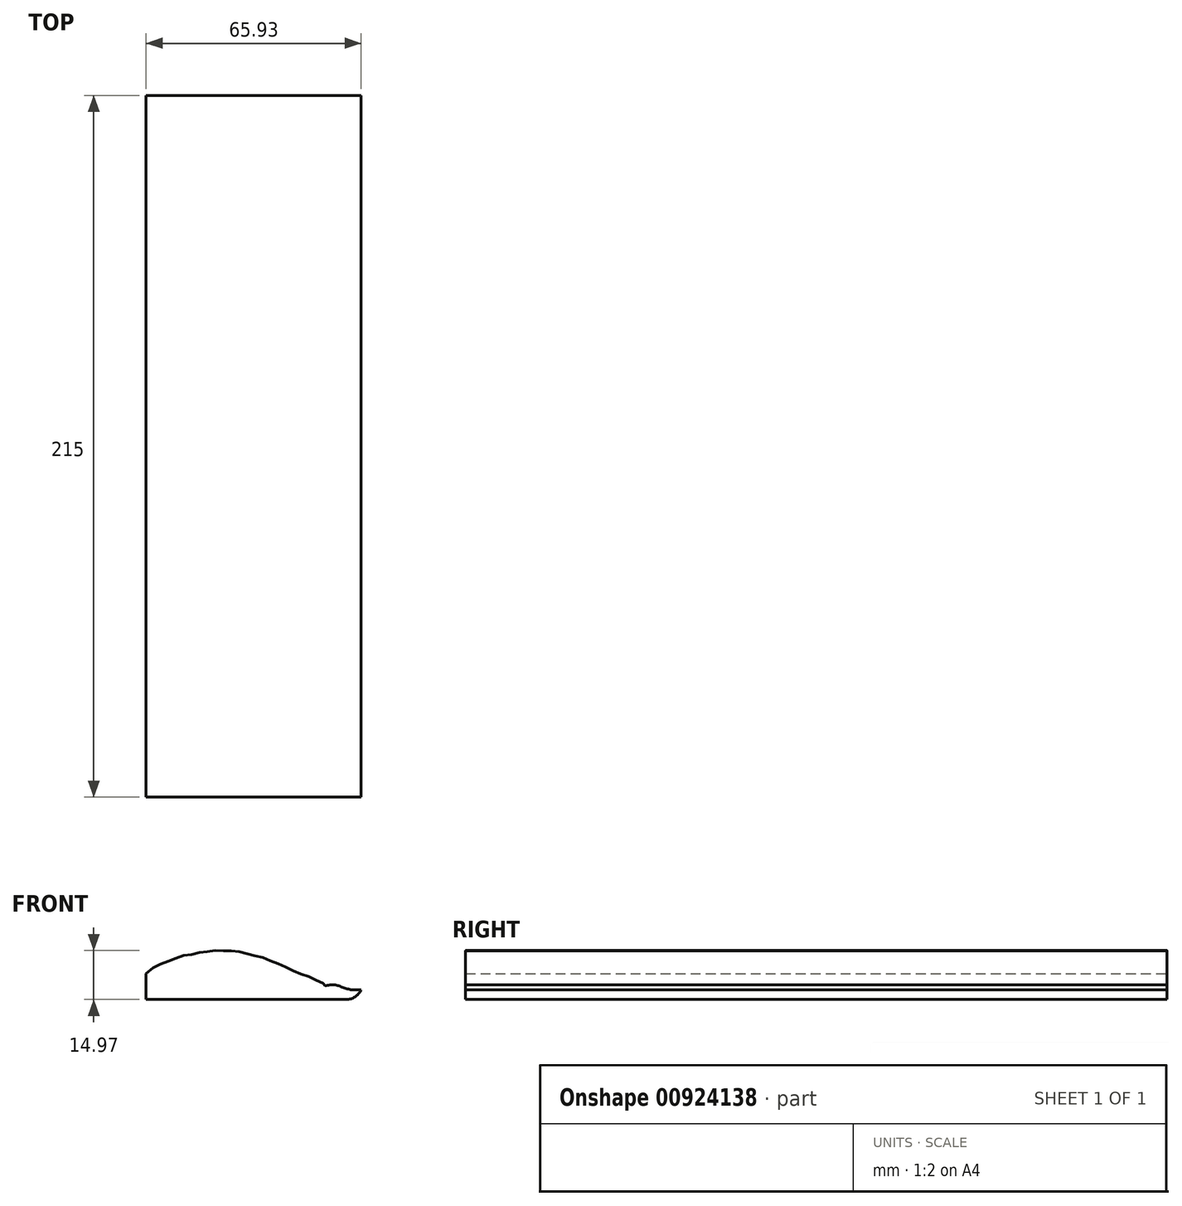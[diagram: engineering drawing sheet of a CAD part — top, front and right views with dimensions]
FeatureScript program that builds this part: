
annotation { "Feature Type Name" : "Feature", "Feature Type Description" : "" }
export const myFeature = defineFeature(function(context is Context, id is Id, definition is map)
    precondition{}
    {
        {
            var Q0;
            Q0=qCreatedBy(makeId("Front.planeOp"),FACE);
            var sketch = newSketch(context, id + "F0", { "sketchPlane" : qUnion([Q0])});
            skLineSegment(sketch, "E0", {"start": v(-70.05, 3) * mm, "end": v(-27.13, 3) * mm, "construction": true});
            skLineSegment(sketch, "E1", {"start": v(-65.4, 11.16) * mm, "end": v(-65.4, 2.2) * mm, "construction": true});
            skLineSegment(sketch, "E2.0", {"start": v(-63.38, 11.16) * mm, "end": v(-63.38, 2.2) * mm, "construction": true});
            skLineSegment(sketch, "E3", {"start": v(-65.9, 7.9) * mm, "end": v(-64.97, 7.9) * mm, "construction": true});
            skPoint(sketch, "E4", {"position": v(-65.4, 7.9) * mm});
            skLineSegment(sketch, "E5", {"start": v(-63.95, 9.66) * mm, "end": v(-62.94, 9.66) * mm, "construction": true});
            skPoint(sketch, "E6", {"position": v(-63.38, 9.66) * mm});
            skLineSegment(sketch, "E7.0", {"start": v(-61.35, 11.16) * mm, "end": v(-61.35, 2.2) * mm, "construction": true});
            skLineSegment(sketch, "E8", {"start": v(-61.84, 10.68) * mm, "end": v(-60.86, 10.68) * mm, "construction": true});
            skPoint(sketch, "E9", {"position": v(-61.35, 10.68) * mm});
            skLineSegment(sketch, "E10.0", {"start": v(-59.32, 11.16) * mm, "end": v(-59.32, 2.2) * mm, "construction": true});
            skLineSegment(sketch, "E11", {"start": v(-59.94, 11.52) * mm, "end": v(-58.72, 11.52) * mm, "construction": true});
            skLineSegment(sketch, "E12", {"start": v(-59.32, 11.16) * mm, "end": v(-59.32, 11.9) * mm, "construction": true});
            skPoint(sketch, "E13", {"position": v(-59.32, 11.52) * mm});
            skLineSegment(sketch, "E14.0", {"start": v(-57.29, 11.16) * mm, "end": v(-57.29, 2.2) * mm, "construction": true});
            skLineSegment(sketch, "E15", {"start": v(-57.8, 12.18) * mm, "end": v(-56.85, 12.18) * mm, "construction": true});
            skLineSegment(sketch, "E16", {"start": v(-57.29, 11.16) * mm, "end": v(-57.29, 12.27) * mm, "construction": true});
            skPoint(sketch, "E17", {"position": v(-57.29, 12.18) * mm});
            skLineSegment(sketch, "E18.0", {"start": v(-55.26, 11.16) * mm, "end": v(-55.26, 2.2) * mm, "construction": true});
            skLineSegment(sketch, "E19", {"start": v(-55.77, 13) * mm, "end": v(-54.8, 13) * mm, "construction": true});
            skLineSegment(sketch, "E20", {"start": v(-55.26, 11.16) * mm, "end": v(-55.26, 15.51) * mm, "construction": true});
            skPoint(sketch, "E21", {"position": v(-55.26, 13) * mm});
            skLineSegment(sketch, "E22.0", {"start": v(-53.23, 11.16) * mm, "end": v(-53.23, 15.51) * mm, "construction": true});
            skLineSegment(sketch, "E23", {"start": v(-53.9, 13.65) * mm, "end": v(-51.58, 13.65) * mm, "construction": true});
            skPoint(sketch, "E24", {"position": v(-53.23, 13.65) * mm});
            skLineSegment(sketch, "E25.0", {"start": v(-51.2, 11.16) * mm, "end": v(-51.2, 15.51) * mm, "construction": true});
            skLineSegment(sketch, "E26", {"start": v(-51.89, 13.77) * mm, "end": v(-50.28, 13.77) * mm, "construction": true});
            skPoint(sketch, "E27", {"position": v(-51.2, 13.77) * mm});
            skLineSegment(sketch, "E28.0", {"start": v(-49.17, 11.16) * mm, "end": v(-49.17, 15.51) * mm, "construction": true});
            skLineSegment(sketch, "E29", {"start": v(-49.78, 14.36) * mm, "end": v(-48.28, 14.36) * mm, "construction": true});
            skPoint(sketch, "E30", {"position": v(-49.17, 14.36) * mm});
            skLineSegment(sketch, "E31.0", {"start": v(-47.14, 11.16) * mm, "end": v(-47.14, 15.51) * mm, "construction": true});
            skLineSegment(sketch, "E32", {"start": v(-48.04, 14.6) * mm, "end": v(-46.3, 14.6) * mm, "construction": true});
            skLineSegment(sketch, "E33", {"start": v(-46.3, 14.6) * mm, "end": v(-46.13, 14.6) * mm, "construction": true});
            skPoint(sketch, "E34", {"position": v(-47.14, 14.6) * mm});
            skLineSegment(sketch, "E35.0", {"start": v(-45.1, 11.16) * mm, "end": v(-45.1, 15.51) * mm, "construction": true});
            skLineSegment(sketch, "E36", {"start": v(-45.76, 14.94) * mm, "end": v(-44.5, 14.94) * mm, "construction": true});
            skPoint(sketch, "E37", {"position": v(-45.1, 14.94) * mm});
            skLineSegment(sketch, "E38.0", {"start": v(-43.08, 11.16) * mm, "end": v(-43.08, 15.51) * mm, "construction": true});
            skLineSegment(sketch, "E39", {"start": v(-43.72, 14.93) * mm, "end": v(-42.54, 14.93) * mm, "construction": true});
            skPoint(sketch, "E40", {"position": v(-43.08, 14.93) * mm});
            skLineSegment(sketch, "E41.0", {"start": v(-41.05, 11.16) * mm, "end": v(-41.05, 15.51) * mm, "construction": true});
            skLineSegment(sketch, "E42", {"start": v(-41.48, 14.92) * mm, "end": v(-40.57, 14.92) * mm, "construction": true});
            skPoint(sketch, "E43", {"position": v(-41.05, 14.92) * mm});
            skLineSegment(sketch, "E44.0", {"start": v(-39.02, 11.16) * mm, "end": v(-39.02, 15.51) * mm, "construction": true});
            skLineSegment(sketch, "E45", {"start": v(-39.51, 14.93) * mm, "end": v(-38.46, 14.93) * mm, "construction": true});
            skPoint(sketch, "E46", {"position": v(-39.02, 14.93) * mm});
            skLineSegment(sketch, "E47.0", {"start": v(-36.99, 11.16) * mm, "end": v(-36.99, 15.51) * mm, "construction": true});
            skLineSegment(sketch, "E48", {"start": v(-37.6, 14.64) * mm, "end": v(-36.43, 14.64) * mm, "construction": true});
            skPoint(sketch, "E49", {"position": v(-36.99, 14.64) * mm});
            skLineSegment(sketch, "E50.0", {"start": v(-34.96, 11.16) * mm, "end": v(-34.96, 15.51) * mm, "construction": true});
            skLineSegment(sketch, "E51", {"start": v(-35.6, 14.18) * mm, "end": v(-34.47, 14.18) * mm, "construction": true});
            skPoint(sketch, "E52", {"position": v(-34.96, 14.18) * mm});
            skLineSegment(sketch, "E53.0", {"start": v(-32.93, 11.16) * mm, "end": v(-32.93, 15.51) * mm, "construction": true});
            skLineSegment(sketch, "E54", {"start": v(-33.65, 13.68) * mm, "end": v(-32.36, 13.68) * mm, "construction": true});
            skPoint(sketch, "E55", {"position": v(-32.93, 13.68) * mm});
            skLineSegment(sketch, "E56.0", {"start": v(-30.9, 11.16) * mm, "end": v(-30.9, 15.51) * mm, "construction": true});
            skLineSegment(sketch, "E57", {"start": v(-31.62, 13.06) * mm, "end": v(-30.17, 13.06) * mm, "construction": true});
            skPoint(sketch, "E58", {"position": v(-30.9, 13.06) * mm});
            skLineSegment(sketch, "E59.0", {"start": v(-28.87, 11.16) * mm, "end": v(-28.87, 15.51) * mm, "construction": true});
            skLineSegment(sketch, "E60", {"start": v(-29.53, 12.63) * mm, "end": v(-28.4, 12.63) * mm, "construction": true});
            skPoint(sketch, "E61", {"position": v(-28.87, 12.63) * mm});
            skLineSegment(sketch, "E62.0", {"start": v(-26.84, 11.16) * mm, "end": v(-26.84, 15.51) * mm, "construction": true});
            skLineSegment(sketch, "E63", {"start": v(-27.43, 11.58) * mm, "end": v(-26.47, 11.58) * mm, "construction": true});
            skLineSegment(sketch, "E64.0", {"start": v(-24.8, 11.16) * mm, "end": v(-24.8, 15.51) * mm, "construction": true});
            skLineSegment(sketch, "E65", {"start": v(-25.6, 10.86) * mm, "end": v(-24, 10.86) * mm, "construction": true});
            skLineSegment(sketch, "E66", {"start": v(-24, 10.86) * mm, "end": v(-24, 11.02) * mm, "construction": true});
            skPoint(sketch, "E67", {"position": v(-26.84, 11.58) * mm});
            skLineSegment(sketch, "E68", {"start": v(-24.8, 11.34) * mm, "end": v(-24.8, 9.73) * mm, "construction": true});
            skPoint(sketch, "E69", {"position": v(-24.8, 10.86) * mm});
            skPoint(sketch, "E70", {"position": v(-26.95, 11.58) * mm});
            skLineSegment(sketch, "E71", {"start": v(-22.78, 10.28) * mm, "end": v(-22.78, 4.3) * mm, "construction": true});
            skLineSegment(sketch, "E72", {"start": v(-23.34, 10.05) * mm, "end": v(-22.08, 10.05) * mm, "construction": true});
            skLineSegment(sketch, "E73", {"start": v(-27.13, 3) * mm, "end": v(-14.06, 3) * mm, "construction": true});
            skPoint(sketch, "E74", {"position": v(-22.78, 10.05) * mm});
            skLineSegment(sketch, "E75.0", {"start": v(-20.75, 10.28) * mm, "end": v(-20.75, 4.3) * mm, "construction": true});
            skLineSegment(sketch, "E76", {"start": v(-21.6, 9) * mm, "end": v(-20.07, 9) * mm, "construction": true});
            skPoint(sketch, "E77", {"position": v(-20.75, 9) * mm});
            skLineSegment(sketch, "E78.0", {"start": v(-18.72, 10.28) * mm, "end": v(-18.72, 4.3) * mm, "construction": true});
            skLineSegment(sketch, "E79", {"start": v(-19.5, 8.1) * mm, "end": v(-18.1, 8.1) * mm, "construction": true});
            skPoint(sketch, "E80", {"position": v(-18.72, 8.1) * mm});
            skLineSegment(sketch, "E81.0", {"start": v(-16.69, 10.28) * mm, "end": v(-16.69, 4.3) * mm, "construction": true});
            skLineSegment(sketch, "E82", {"start": v(-17.25, 7.25) * mm, "end": v(-16.32, 7.25) * mm, "construction": true});
            skPoint(sketch, "E83", {"position": v(-16.69, 7.25) * mm});
            skPoint(sketch, "E84", {"position": v(-15.54, 8.12) * mm});
            skLineSegment(sketch, "E85.0", {"start": v(-14.66, 10.28) * mm, "end": v(-14.66, 4.3) * mm, "construction": true});
            skLineSegment(sketch, "E86", {"start": v(-15.25, 6.77) * mm, "end": v(-14.02, 6.77) * mm, "construction": true});
            skPoint(sketch, "E87", {"position": v(-14.66, 6.77) * mm});
            skLineSegment(sketch, "E88", {"start": v(-14.06, 3) * mm, "end": v(-2.16, 3) * mm, "construction": true});
            skLineSegment(sketch, "E89.0", {"start": v(-12.63, 10.28) * mm, "end": v(-12.63, 4.3) * mm, "construction": true});
            skLineSegment(sketch, "E90", {"start": v(-13.45, 5.53) * mm, "end": v(-11.88, 5.53) * mm, "construction": true});
            skPoint(sketch, "E91", {"position": v(-12.63, 5.53) * mm});
            skLineSegment(sketch, "E92.0", {"start": v(-10.6, 10.28) * mm, "end": v(-10.6, 4.3) * mm, "construction": true});
            skLineSegment(sketch, "E93", {"start": v(-11.21, 5) * mm, "end": v(-10.03, 5) * mm, "construction": true});
            skPoint(sketch, "E94", {"position": v(-10.6, 5) * mm});
            skLineSegment(sketch, "E95", {"start": v(-8.57, 6.03) * mm, "end": v(-8.57, 1.25) * mm, "construction": true});
            skLineSegment(sketch, "E96", {"start": v(-9.47, 4.52) * mm, "end": v(-7.87, 4.52) * mm, "construction": true});
            skPoint(sketch, "E97", {"position": v(-8.57, 4.52) * mm});
            skLineSegment(sketch, "E98.0", {"start": v(-6.54, 6.03) * mm, "end": v(-6.54, 1.25) * mm, "construction": true});
            skLineSegment(sketch, "E99", {"start": v(-7.13, 4.25) * mm, "end": v(-5.96, 4.25) * mm, "construction": true});
            skPoint(sketch, "E100", {"position": v(-6.54, 4.25) * mm});
            skLineSegment(sketch, "E101.0", {"start": v(-4.5, 6.03) * mm, "end": v(-4.5, 1.25) * mm, "construction": true});
            skLineSegment(sketch, "E102", {"start": v(-5.09, 3.5) * mm, "end": v(-4.09, 3.5) * mm, "construction": true});
            skPoint(sketch, "E103", {"position": v(-4.5, 3.5) * mm});
            skLineSegment(sketch, "E104.0", {"start": v(-2.48, 6.03) * mm, "end": v(-2.48, 1.25) * mm, "construction": true});
            skPoint(sketch, "E105", {"position": v(-2.48, 3) * mm});
            skLineSegment(sketch, "E106", {"start": v(-2.9, 3) * mm, "end": v(5.51, 3) * mm, "construction": true});
            skLineSegment(sketch, "E107.0", {"start": v(0.52, 6.03) * mm, "end": v(0.52, 1.25) * mm, "construction": true});
            skPoint(sketch, "E108", {"position": v(0.52, 3) * mm});
            skPoint(sketch, "E109", {"position": v(-51.9, 8.5) * mm});
            skFitSpline(sketch, "E110", {"points": [v(-65.4, 7.9) * mm, v(-63.38, 9.66) * mm, v(-61.35, 10.68) * mm, v(-59.32, 11.52) * mm, v(-57.29, 12.27) * mm, v(-55.26, 13) * mm, v(-53.23, 13.65) * mm, v(-51.2, 13.77) * mm, v(-49.17, 14.36) * mm, v(-47.14, 14.6) * mm, v(-45.1, 14.94) * mm, v(-43.08, 14.93) * mm, v(-41.05, 14.92) * mm, v(-39.02, 14.93) * mm, v(-36.99, 14.64) * mm, v(-34.96, 14.18) * mm, v(-32.93, 13.68) * mm, v(-30.9, 13.06) * mm, v(-28.87, 12.63) * mm, v(-26.84, 11.58) * mm, v(-24.8, 10.86) * mm, v(-22.78, 10.05) * mm, v(-20.75, 9) * mm, v(-18.72, 8.1) * mm, v(-16.69, 7.25) * mm, v(-14.66, 6.77) * mm, v(-12.63, 5.53) * mm, v(-11.21, 5) * mm, v(-10.6, 4.3) * mm, v(-10.2, 4.25) * mm, v(-8.57, 4.52) * mm, v(-6.54, 4.25) * mm, v(-4.5, 3.5) * mm, v(-2.48, 3) * mm, v(0.52, 3) * mm], "startDerivative": vector(58.64, 57.04) * mm, "endDerivative": vector(136.63, 4.4) * mm});
            skLineSegment(sketch, "E111", {"start": v(0.52, 3) * mm, "end": v(0.52, 0) * mm});
            skLineSegment(sketch, "E112", {"start": v(0.52, 0) * mm, "end": v(-65.4, 0) * mm});
            skLineSegment(sketch, "E113", {"start": v(-65.4, 7.9) * mm, "end": v(-65.4, 0) * mm});
            skLineSegment(sketch, "E114", {"start": v(-11.21, 5) * mm, "end": v(-8.57, 4.52) * mm});
            skSolve(sketch);
        }
        {
            var Q0;
            {var subQ0=sQuery(id+"F0.wireOp",EDGE,"E111");Q0=makeQuery(id+"F0.imprint","IMPRINT",FACE,{"disambiguationData":[TD([[makeQuery(id+"F0.imprint","IMPRINT",EDGE,{"derivedFrom":subQ0}),-1.0]])]});}
            extrude(context, id + "F1", {"entities" : qUnion([Q0]), "depth" : 215 * mm, "offsetDistance" : 25 * mm});
        }
        {
            var Q0;
            Q0=makeQuery(id+"F1.opExtrude","SWEPT_EDGE",EDGE,{"disambiguationData":[OSD([sQuery(id+"F0.wireOp",EDGE,"E111"),sQuery(id+"F0.wireOp",EDGE,"E112")])]});
            fillet(context, id + "F2", {"entities" : qUnion([Q0]), "radius" : 5 * mm, "tangentPropagation" : true, "allowEdgeOverflow" : false});
        }
    });
